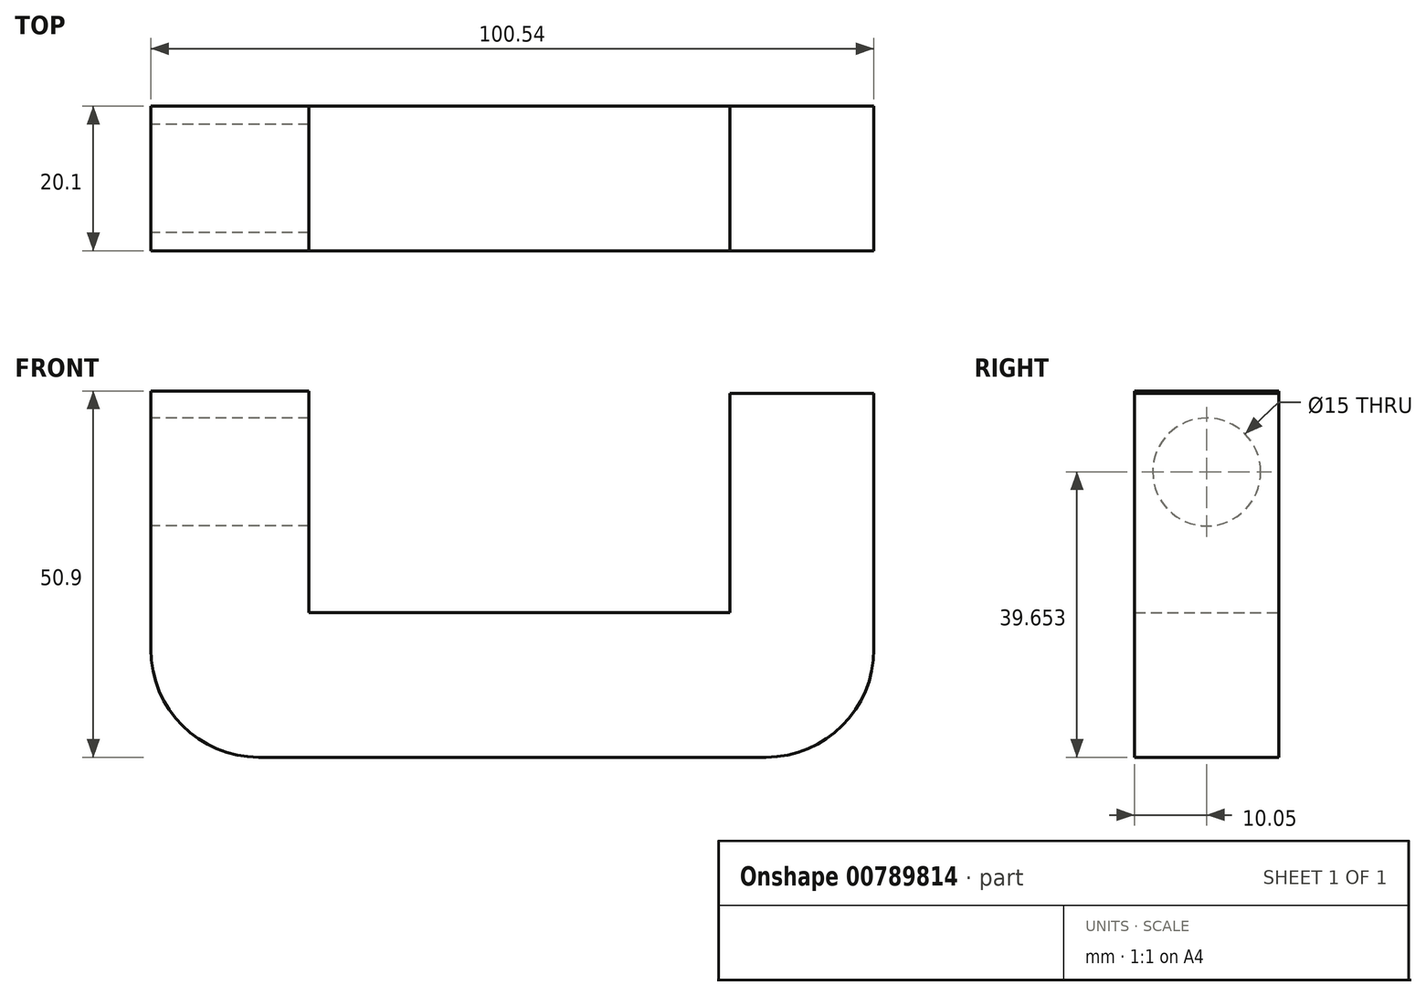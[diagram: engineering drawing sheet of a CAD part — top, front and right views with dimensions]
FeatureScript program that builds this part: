
annotation { "Feature Type Name" : "Feature", "Feature Type Description" : "" }
export const myFeature = defineFeature(function(context is Context, id is Id, definition is map)
    precondition{}
    {
        {
            var Q0;
            Q0=qCreatedBy(makeId("Front.planeOp"),FACE);
            var sketch = newSketch(context, id + "F0", { "sketchPlane" : qUnion([Q0])});
            skLineSegment(sketch, "E0", {"start": v(-19.68, -8.2) * mm, "end": v(50.86, -8.2) * mm});
            skLineSegment(sketch, "E1", {"start": v(65.86, 6.8) * mm, "end": v(65.86, 42.35) * mm});
            skLineSegment(sketch, "E2", {"start": v(45.86, 42.35) * mm, "end": v(45.86, 11.9) * mm});
            skLineSegment(sketch, "E3", {"start": v(45.86, 11.9) * mm, "end": v(-12.68, 11.9) * mm});
            skLineSegment(sketch, "E4", {"start": v(45.86, 42.35) * mm, "end": v(65.86, 42.35) * mm});
            skLineSegment(sketch, "E5", {"start": v(-12.68, 11.9) * mm, "end": v(-12.68, 42.7) * mm});
            skLineSegment(sketch, "E6", {"start": v(-12.68, 42.7) * mm, "end": v(-34.68, 42.7) * mm});
            skLineSegment(sketch, "E7", {"start": v(-34.68, 42.7) * mm, "end": v(-34.68, 6.8) * mm});
            skPoint(sketch, "E8.visualSharp", {"position": v(-34.68, -8.2) * mm});
            skArc(sketch, "E8.filletArc", {"start": v(-34.68, 6.8) * mm, "mid": v(-30.28, -3.8) * mm, "end": v(-19.68, -8.2) * mm});
            skPoint(sketch, "E9.visualSharp", {"position": v(65.86, -8.2) * mm});
            skArc(sketch, "E9.filletArc", {"start": v(50.86, -8.2) * mm, "mid": v(61.47, -3.8) * mm, "end": v(65.86, 6.8) * mm});
            skSolve(sketch);
        }
        {
            var Q0;
            Q0=makeQuery(id+"F0.imprint","IMPRINT",FACE,{"disambiguationData":[TD([[makeQuery(id+"F0.imprint","IMPRINT",EDGE,{"derivedFrom":sQuery(id+"F0.wireOp",EDGE,"E0")}),1.0]])]});
            extrude(context, id + "F1", {"entities" : qUnion([Q0]), "endBound" : BoundingType.SYMMETRIC, "depth" : 20.1 * mm, "offsetDistance" : 25 * mm});
        }
        {
            var Q0;
            Q0=makeQuery(id+"F1.opExtrude","SWEPT_FACE",FACE,{"disambiguationData":[OSD([sQuery(id+"F0.wireOp",EDGE,"E7")])]});
            var sketch = newSketch(context, id + "F2", { "sketchPlane" : qUnion([Q0])});
            skCircle(sketch, "E10", {"center": v(0, 31.45) * mm, "radius": 7.5 * mm});
            skPoint(sketch, "E10.centerSnap0", {"position": v(0, 42.7) * mm});
            skSolve(sketch);
        }
        {
            var Q0;
            Q0=makeQuery(id+"F2.imprint","IMPRINT",FACE,{"disambiguationData":[TD([[makeQuery(id+"F2.imprint","IMPRINT",EDGE,{"derivedFrom":sQuery(id+"F2.wireOp",EDGE,"E10")}),1.0]])]});
            extrude(context, id + "F3", {"entities" : qUnion([Q0]), "operationType" : NewBodyOperationType.REMOVE, "oppositeDirection" : true, "depth" : 25 * mm, "offsetDistance" : 25 * mm});
        }
    });
